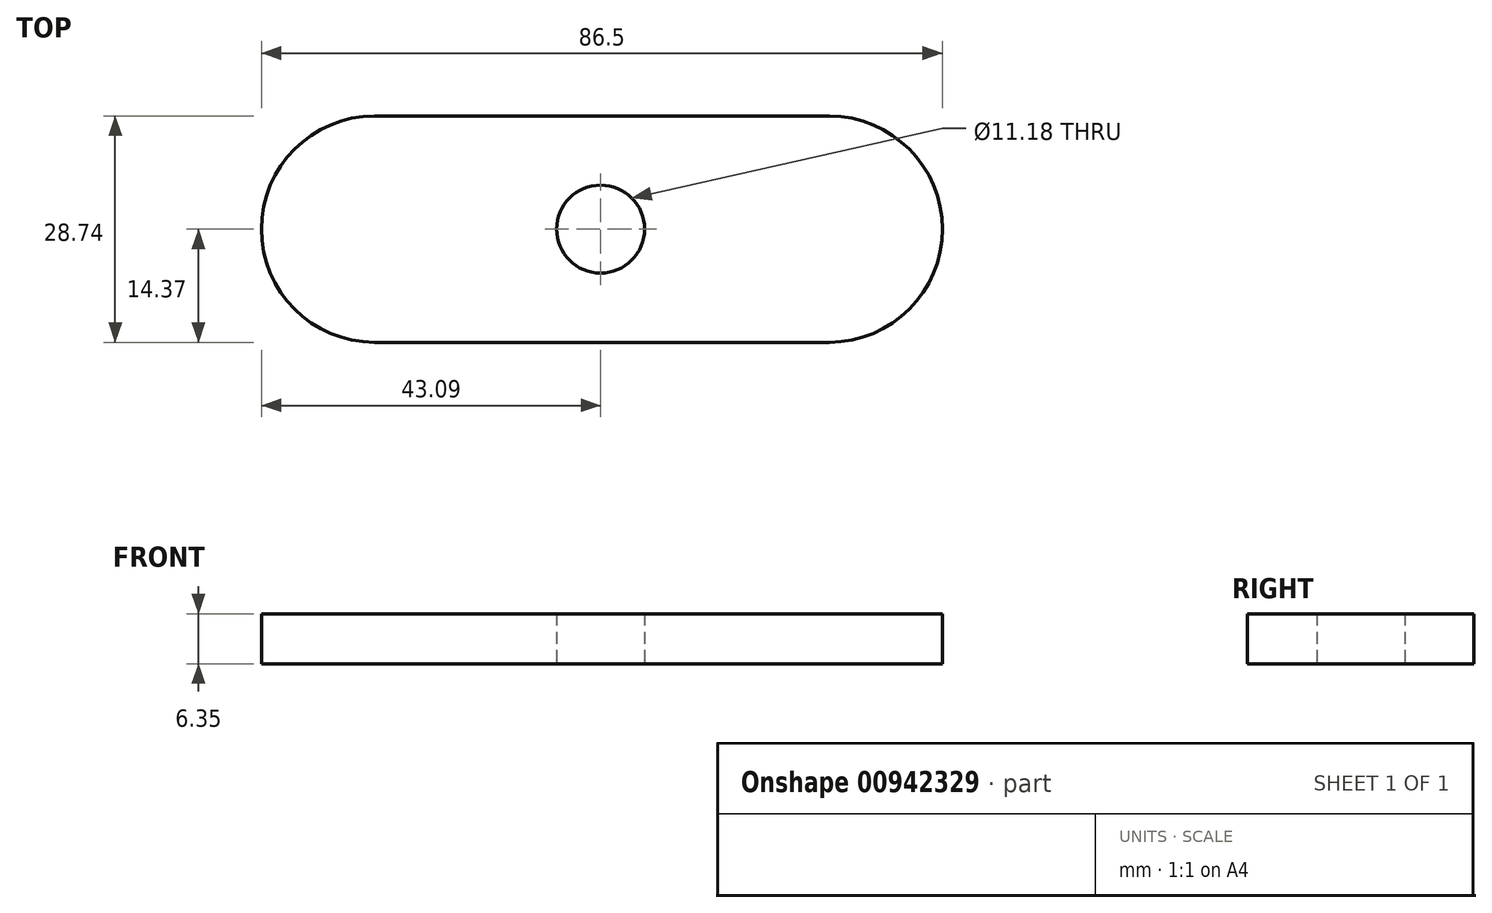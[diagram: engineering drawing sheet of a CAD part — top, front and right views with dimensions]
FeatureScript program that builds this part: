
annotation { "Feature Type Name" : "Feature", "Feature Type Description" : "" }
export const myFeature = defineFeature(function(context is Context, id is Id, definition is map)
    precondition{}
    {
        {
            var Q0;
            Q0=qCreatedBy(makeId("Top.planeOp"),FACE);
            var sketch = newSketch(context, id + "F0", { "sketchPlane" : qUnion([Q0])});
            skCircle(sketch, "E0", {"center": v(0, 0) * mm, "radius": 5.59 * mm});
            skLineSegment(sketch, "E1.bottom", {"start": v(-28.72, 14.37) * mm, "end": v(29.04, 14.37) * mm});
            skLineSegment(sketch, "E1.top", {"start": v(-28.72, -14.37) * mm, "end": v(29.04, -14.37) * mm});
            skLineSegment(sketch, "E1.left", {"start": v(-28.72, 14.37) * mm, "end": v(-28.72, -14.37) * mm});
            skLineSegment(sketch, "E1.right", {"start": v(29.04, 14.37) * mm, "end": v(29.04, -14.37) * mm});
            skCircle(sketch, "E2", {"center": v(-28.72, 0) * mm, "radius": 14.37 * mm});
            skCircle(sketch, "E3", {"center": v(29.04, 0) * mm, "radius": 14.37 * mm});
            skCircle(sketch, "E4", {"center": v(29.04, 0) * mm, "radius": 10.99 * mm});
            skCircle(sketch, "E5", {"center": v(-28.72, 0) * mm, "radius": 10.99 * mm});
            skSolve(sketch);
        }
        {
            var Q0;
            {var subQ1=sQuery(id+"F0.wireOp",EDGE,"E1.right");var subQ3=sQuery(id+"F0.wireOp",EDGE,"E4");var subQ4=makeQuery(id+"F0.imprint","INTERSECT",VERTEX,{"disambiguationData":[OD(0.0)],"derivedFrom":[subQ1,subQ3]});Q0=makeQuery(id+"F0.imprint","IMPRINT",FACE,{"disambiguationData":[TD([[makeQuery(id+"F0.imprint","IMPRINT",EDGE,{"disambiguationData":[TD([[subQ4,-1.0]])],"derivedFrom":subQ3}),-1.0]])]});}
            var Q1;
            {var subQ0=sQuery(id+"F0.wireOp",EDGE,"E4");var subQ1=sQuery(id+"F0.wireOp",EDGE,"E1.right");var subQ2=makeQuery(id+"F0.imprint","INTERSECT",VERTEX,{"disambiguationData":[OD(0.0)],"derivedFrom":[subQ1,subQ0]});Q1=makeQuery(id+"F0.imprint","IMPRINT",FACE,{"disambiguationData":[TD([[makeQuery(id+"F0.imprint","IMPRINT",EDGE,{"disambiguationData":[TD([[subQ2,-1.0]])],"derivedFrom":subQ1}),1.0]])]});}
            var Q2;
            {var subQ1=sQuery(id+"F0.wireOp",EDGE,"E1.right");var subQ3=sQuery(id+"F0.wireOp",EDGE,"E4");var subQ4=makeQuery(id+"F0.imprint","INTERSECT",VERTEX,{"disambiguationData":[OD(0.0)],"derivedFrom":[subQ1,subQ3]});Q2=makeQuery(id+"F0.imprint","IMPRINT",FACE,{"disambiguationData":[TD([[makeQuery(id+"F0.imprint","IMPRINT",EDGE,{"disambiguationData":[TD([[subQ4,1.0]])],"derivedFrom":subQ3}),-1.0]])]});}
            var Q3;
            {var subQ0=sQuery(id+"F0.wireOp",EDGE,"E4");var subQ1=sQuery(id+"F0.wireOp",EDGE,"E1.right");var subQ2=makeQuery(id+"F0.imprint","INTERSECT",VERTEX,{"disambiguationData":[OD(0.0)],"derivedFrom":[subQ1,subQ0]});Q3=makeQuery(id+"F0.imprint","IMPRINT",FACE,{"disambiguationData":[TD([[makeQuery(id+"F0.imprint","IMPRINT",EDGE,{"disambiguationData":[TD([[subQ2,-1.0]])],"derivedFrom":subQ1}),-1.0]])]});}
            var Q4;
            {var subQ1=sQuery(id+"F0.wireOp",EDGE,"E1.left");var subQ3=sQuery(id+"F0.wireOp",EDGE,"E5");var subQ4=makeQuery(id+"F0.imprint","INTERSECT",VERTEX,{"disambiguationData":[OD(0.0)],"derivedFrom":[subQ1,subQ3]});Q4=makeQuery(id+"F0.imprint","IMPRINT",FACE,{"disambiguationData":[TD([[makeQuery(id+"F0.imprint","IMPRINT",EDGE,{"disambiguationData":[TD([[subQ4,1.0]])],"derivedFrom":subQ3}),-1.0]])]});}
            var Q5;
            {var subQ0=sQuery(id+"F0.wireOp",EDGE,"E5");var subQ1=sQuery(id+"F0.wireOp",EDGE,"E1.left");var subQ2=makeQuery(id+"F0.imprint","INTERSECT",VERTEX,{"disambiguationData":[OD(0.0)],"derivedFrom":[subQ1,subQ0]});Q5=makeQuery(id+"F0.imprint","IMPRINT",FACE,{"disambiguationData":[TD([[makeQuery(id+"F0.imprint","IMPRINT",EDGE,{"disambiguationData":[TD([[subQ2,-1.0]])],"derivedFrom":subQ1}),-1.0]])]});}
            var Q6;
            {var subQ1=sQuery(id+"F0.wireOp",EDGE,"E1.left");var subQ3=sQuery(id+"F0.wireOp",EDGE,"E5");var subQ4=makeQuery(id+"F0.imprint","INTERSECT",VERTEX,{"disambiguationData":[OD(0.0)],"derivedFrom":[subQ1,subQ3]});Q6=makeQuery(id+"F0.imprint","IMPRINT",FACE,{"disambiguationData":[TD([[makeQuery(id+"F0.imprint","IMPRINT",EDGE,{"disambiguationData":[TD([[subQ4,-1.0]])],"derivedFrom":subQ3}),-1.0]])]});}
            var Q7;
            {var subQ0=sQuery(id+"F0.wireOp",EDGE,"E5");var subQ1=sQuery(id+"F0.wireOp",EDGE,"E1.left");var subQ2=makeQuery(id+"F0.imprint","INTERSECT",VERTEX,{"disambiguationData":[OD(0.0)],"derivedFrom":[subQ1,subQ0]});Q7=makeQuery(id+"F0.imprint","IMPRINT",FACE,{"disambiguationData":[TD([[makeQuery(id+"F0.imprint","IMPRINT",EDGE,{"disambiguationData":[TD([[subQ2,-1.0]])],"derivedFrom":subQ1}),1.0]])]});}
            var Q8;
            Q8=makeQuery(id+"F0.imprint","IMPRINT",FACE,{"disambiguationData":[TD([[makeQuery(id+"F0.imprint","IMPRINT",EDGE,{"derivedFrom":sQuery(id+"F0.wireOp",EDGE,"E0")}),-1.0]])]});
            extrude(context, id + "F1", {"entities" : qUnion([Q0, Q1, Q2, Q3, Q4, Q5, Q6, Q7, Q8]), "depth" : 6.35 * mm, "offsetDistance" : 25.4 * mm});
        }
    });
